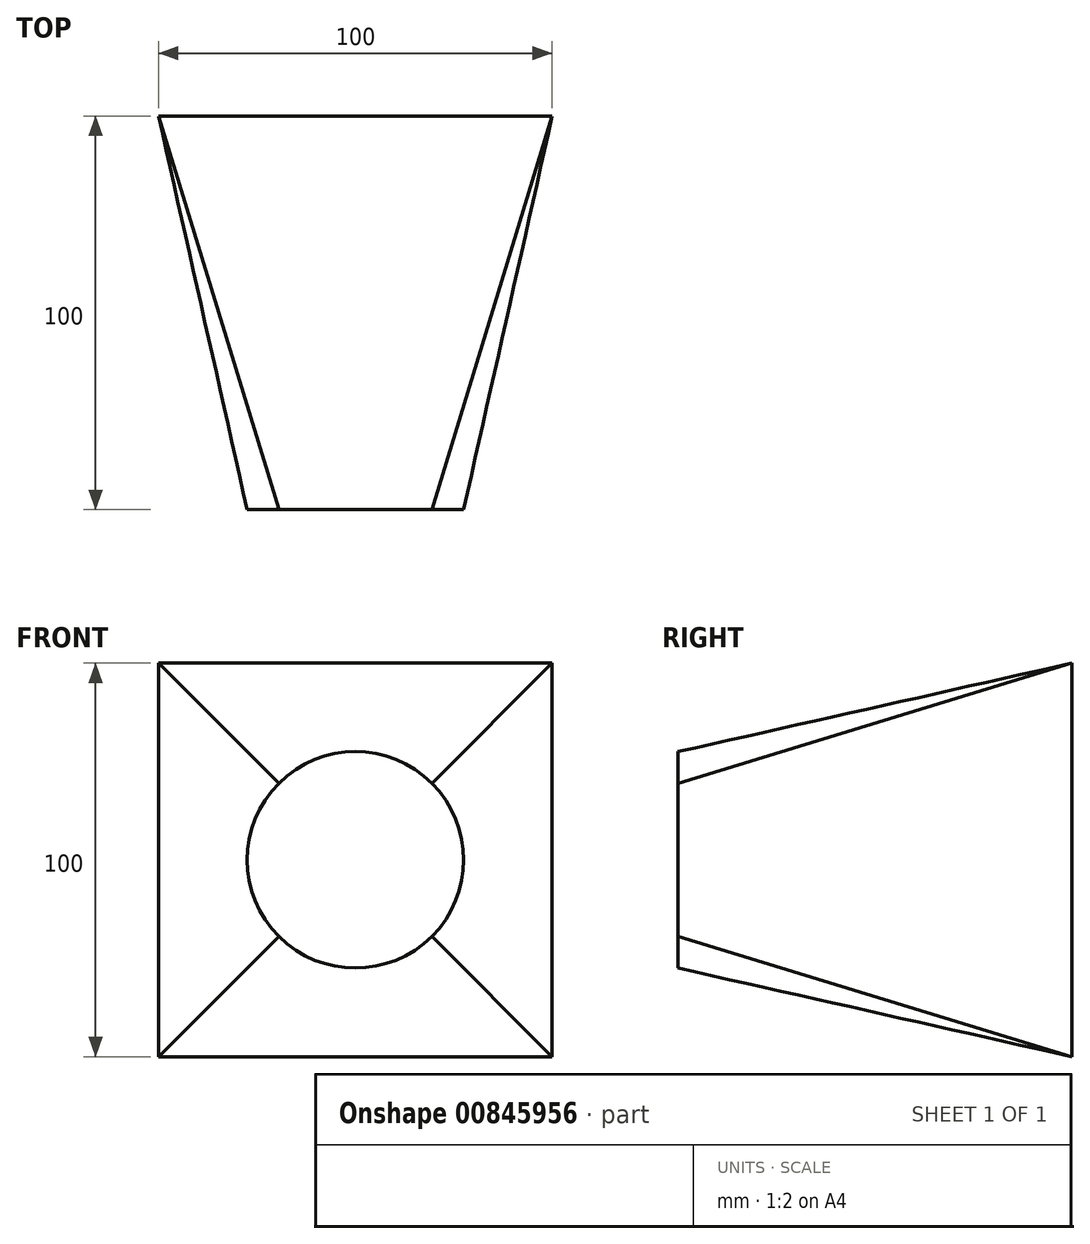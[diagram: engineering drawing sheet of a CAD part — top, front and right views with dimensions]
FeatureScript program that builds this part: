
annotation { "Feature Type Name" : "Feature", "Feature Type Description" : "" }
export const myFeature = defineFeature(function(context is Context, id is Id, definition is map)
    precondition{}
    {
        {
            var Q0;
            Q0=qCreatedBy(makeId("Front.planeOp"),FACE);
            var sketch = newSketch(context, id + "F0", { "sketchPlane" : qUnion([Q0])});
            skLineSegment(sketch, "E0.bottom", {"start": v(50, -50) * mm, "end": v(-50, -50) * mm});
            skLineSegment(sketch, "E0.top", {"start": v(50, 50) * mm, "end": v(-50, 50) * mm});
            skLineSegment(sketch, "E0.left", {"start": v(50, -50) * mm, "end": v(50, 50) * mm});
            skLineSegment(sketch, "E0.right", {"start": v(-50, -50) * mm, "end": v(-50, 50) * mm});
            skPoint(sketch, "E0.middle", {"position": v(0, 0) * mm});
            skSolve(sketch);
        }
        {
            var Q0;
            Q0=qCreatedBy(makeId("Front.planeOp"),FACE);
            cPlane(context, id + "F1", {"entities" : qUnion([Q0]), "cplaneType" : CPlaneType.OFFSET, "offset" : 100 * mm, "width" : 150 * mm, "height" : 150 * mm});
        }
        {
            var Q0;
            Q0=qCreatedBy(id+"F1.planeOp",FACE);
            var sketch = newSketch(context, id + "F2", { "sketchPlane" : qUnion([Q0])});
            skCircle(sketch, "E1", {"center": v(0, 0) * mm, "radius": 27.5 * mm});
            skSolve(sketch);
        }
        {
            var Q0;
            Q0=makeQuery(id+"F0.imprint","IMPRINT",FACE,{"disambiguationData":[TD([[makeQuery(id+"F0.imprint","IMPRINT",EDGE,{"derivedFrom":sQuery(id+"F0.wireOp",EDGE,"E0.bottom")}),-1.0]])]});
            var Q1;
            Q1=makeQuery(id+"F2.imprint","IMPRINT",FACE,{"disambiguationData":[TD([[makeQuery(id+"F2.imprint","IMPRINT",EDGE,{"derivedFrom":sQuery(id+"F2.wireOp",EDGE,"E1")}),1.0]])]});
            loft(context, id + "F3", {"curveCount" : 10, "sheetProfilesArray" : [{ "sheetProfileEntities" : qUnion([Q0]) }, { "sheetProfileEntities" : qUnion([Q1]) }], "trimGuidesByProfiles" : true});
        }
    });
